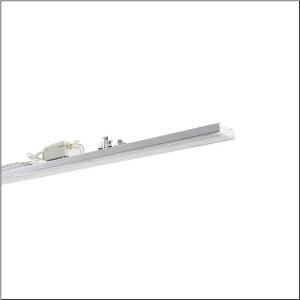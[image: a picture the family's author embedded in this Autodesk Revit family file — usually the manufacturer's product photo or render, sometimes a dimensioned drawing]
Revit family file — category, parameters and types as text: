
# Revit family: licross_r__21_recessed_mo_52tl19mn4a5g_a44e
name_source: partatom
category: Lighting Fixtures
units: mm (PartAtom-declared; Revit-internal decimal feet)

## family parameters
Cut with Voids When Loaded = No
Host = Face
Light Source = No
Part Type = Normal
Room Calculation Point = No
Round Connector Dimension = Use Diameter
Shared = No

## types (1)
- --- (1 x LED, 10530 lm, 60.5 W, 4000K)
    Apparent Load = 61 VA
    CIE Flux Codes = 55 90 98 100 100
    Color Rendering = 80
    Color Temperature = 4000K
    Default Elevation = 1800 mm
    Description = Licross® 21 Recessed MO, luminaire insert, of sheet steel, galvanised, coil coated, white, length: 1.500mm, width: 66mm, height: 67mm, LED rated luminous flux: 10.530lm, light colour: 840, control gear: ON/OFF Multilumen, with plug, 3-pole, with phase selection, mains connection: 220..240V, AC, 50/60Hz, rated input power: 61W, halogen-free wiring, primary light control with lens, of plastic, primary optical cover: cover, of PMMA, light emission: direct distribution, primary light characteristic: double asymmetric, protection rating (complete): IP40, insulation class (complete): insulation class I (protective earthing), certification: CE, ENEC, VDE, UKCA, protection symbol: D if used in an environment without relevant dust loads with corresponding accessories, impact resistance: IK06, permissible ambient temperature for indoor applications: -35..+40°C, corresponds to IFS (International Featured Standards) requirements for safety and quality in the food industry, reducing of maximum allowable ambient temperature of 5°C with ceiling mounting, LABS conformity tested according to VDMA 24364:2018-05, packaging unit: 1 piece
    Height = 58 mm
    Lamp = 1 x LED
    Lamp Light Flux = 10530 lm
    Lamp Power = 60.5 W
    Lamp count = 1
    Length = 1500 mm
    Luminous efficacy = 174 lm/W
    Manufacturer = Siteco
    ModVariant = No
    Model = 52TL19MN4A5G
    Mounting Place = Ceiling
    Mounting Type = Pendant
    Number of Poles = 1
    OnlyDefault = Yes
    Power Factor = 1
    Product Name = Licross® 21 Recessed MO
    Product group = luminaire insert
    ProductGroupID = 901
    Protection Class = Protection class I
    Protection Degree = IP 40
    RLX_Detail_Level = 1
    RLX_Emergency_Light_Flux = 0 lm
    RLX_Emergency_Type = 0
    RLX_Emergency_Type_DB = No
    RlxData = <blob elided: 22245 chars, md5=fe5e194e>
    Socket = socket
    Standby Power = 0 W
    System Light Flux = 10530 lm
    System Power = 61 W
    Type Comments = factory setting: luminous flux: 100 % | (A | C | E) | 140 mA
    Type Image = l_1296930.jpg
    URL = http://relux.com
    VarID = @adj_039141
    Voltage = 0 V
    Weight = 0.00 kg
    Width = 66 mm

## geometry (parser evidence)
native form markers: Blend x4, Sweep x9
no freeform markers — native parametric forms only
